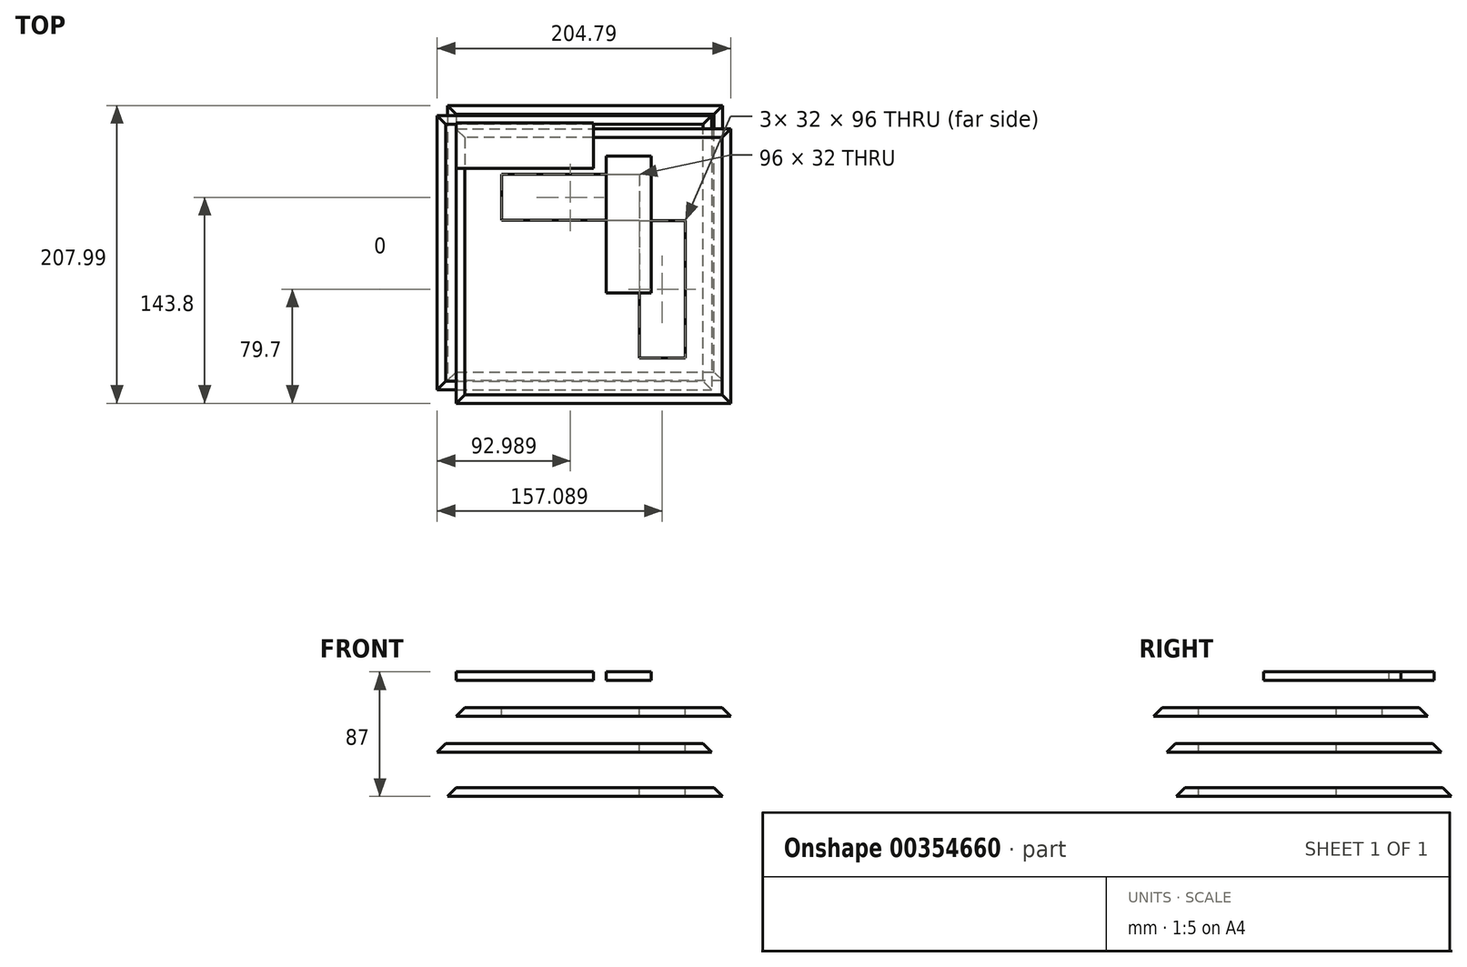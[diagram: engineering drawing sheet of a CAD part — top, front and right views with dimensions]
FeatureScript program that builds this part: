
annotation { "Feature Type Name" : "Feature", "Feature Type Description" : "" }
export const myFeature = defineFeature(function(context is Context, id is Id, definition is map)
    precondition{}
    {
        {
            var Q0;
            Q0=qCreatedBy(makeId("Top.planeOp"),FACE);
            var sketch = newSketch(context, id + "F0", { "sketchPlane" : qUnion([Q0])});
            skLineSegment(sketch, "E0.bottom", {"start": v(-110.78, 83.07) * mm, "end": v(81.22, 83.07) * mm});
            skLineSegment(sketch, "E0.top", {"start": v(-110.78, -108.93) * mm, "end": v(81.22, -108.93) * mm});
            skLineSegment(sketch, "E0.left", {"start": v(-110.78, 83.07) * mm, "end": v(-110.78, -108.93) * mm});
            skLineSegment(sketch, "E0.right", {"start": v(81.22, 83.07) * mm, "end": v(81.22, -108.93) * mm});
            skSolve(sketch);
        }
        {
            var Q0;
            Q0=makeQuery(id+"F0.imprint","IMPRINT",FACE,{"disambiguationData":[TD([[makeQuery(id+"F0.imprint","IMPRINT",EDGE,{"derivedFrom":sQuery(id+"F0.wireOp",EDGE,"E0.bottom")}),-1.0]])]});
            extrude(context, id + "F1", {"entities" : qUnion([Q0]), "depth" : 6 * mm});
        }
        {
            var Q0;
            Q0=makeQuery(id+"F1.opExtrude","CAP_FACE",FACE,{"disambiguationData":[OSD([sQuery(id+"F0.wireOp",EDGE,"E0.bottom"),sQuery(id+"F0.wireOp",EDGE,"E0.top"),sQuery(id+"F0.wireOp",EDGE,"E0.left"),sQuery(id+"F0.wireOp",EDGE,"E0.right")])],"isStart":false});
            chamfer(context, id + "F2", {"entities" : qUnion([Q0]), "width" : 6 * mm, "tangentPropagation" : true});
        }
        {
            var Q0;
            Q0=makeQuery(id+"F1.opExtrude","CAP_FACE",FACE,{"disambiguationData":[OSD([sQuery(id+"F0.wireOp",EDGE,"E0.bottom"),sQuery(id+"F0.wireOp",EDGE,"E0.top"),sQuery(id+"F0.wireOp",EDGE,"E0.left"),sQuery(id+"F0.wireOp",EDGE,"E0.right")])],"isStart":false});
            cPlane(context, id + "F3", {"entities" : qUnion([Q0]), "cplaneType" : CPlaneType.OFFSET, "offset" : 25 * mm, "width" : 150 * mm, "height" : 150 * mm});
        }
        {
            var Q0;
            Q0=qCreatedBy(id+"F3.planeOp",FACE);
            var sketch = newSketch(context, id + "F4", { "sketchPlane" : qUnion([Q0])});
            skLineSegment(sketch, "E1.bottom", {"start": v(-118.07, 76.11) * mm, "end": v(73.53, 76.11) * mm});
            skLineSegment(sketch, "E1.top", {"start": v(-118.07, -115.49) * mm, "end": v(73.53, -115.49) * mm});
            skLineSegment(sketch, "E1.left", {"start": v(-118.07, 76.11) * mm, "end": v(-118.07, -115.49) * mm});
            skLineSegment(sketch, "E1.right", {"start": v(73.53, 76.11) * mm, "end": v(73.53, -115.49) * mm});
            skSolve(sketch);
        }
        {
            var Q0;
            Q0=makeQuery(id+"F4.imprint","IMPRINT",FACE,{"disambiguationData":[TD([[makeQuery(id+"F4.imprint","IMPRINT",EDGE,{"derivedFrom":sQuery(id+"F4.wireOp",EDGE,"E1.bottom")}),-1.0]])]});
            extrude(context, id + "F5", {"entities" : qUnion([Q0]), "depth" : 6 * mm});
        }
        {
            var Q0;
            Q0=makeQuery(id+"F5.opExtrude","CAP_FACE",FACE,{"disambiguationData":[OSD([sQuery(id+"F4.wireOp",EDGE,"E1.bottom"),sQuery(id+"F4.wireOp",EDGE,"E1.top"),sQuery(id+"F4.wireOp",EDGE,"E1.left"),sQuery(id+"F4.wireOp",EDGE,"E1.right")])],"isStart":false});
            chamfer(context, id + "F6", {"entities" : qUnion([Q0]), "width" : 6 * mm, "tangentPropagation" : true});
        }
        {
            var Q0;
            Q0=qCreatedBy(id+"F3.planeOp",FACE);
            cPlane(context, id + "F7", {"entities" : qUnion([Q0]), "cplaneType" : CPlaneType.OFFSET, "offset" : 25 * mm, "width" : 150 * mm, "height" : 150 * mm});
        }
        {
            var Q0;
            Q0=qCreatedBy(id+"F7.planeOp",FACE);
            var sketch = newSketch(context, id + "F8", { "sketchPlane" : qUnion([Q0])});
            skLineSegment(sketch, "E2.bottom", {"start": v(-104.88, 66.68) * mm, "end": v(86.72, 66.68) * mm});
            skLineSegment(sketch, "E2.top", {"start": v(-104.88, -124.92) * mm, "end": v(86.72, -124.92) * mm});
            skLineSegment(sketch, "E2.left", {"start": v(-104.88, 66.68) * mm, "end": v(-104.88, -124.92) * mm});
            skLineSegment(sketch, "E2.right", {"start": v(86.72, 66.68) * mm, "end": v(86.72, -124.92) * mm});
            skSolve(sketch);
        }
        {
            var Q0;
            Q0 = qSketchRegion(id + "F8", true);
            extrude(context, id + "F9", {"entities" : qUnion([Q0]), "depth" : 6 * mm});
        }
        {
            var Q0;
            Q0=makeQuery(id+"F9.opExtrude","CAP_FACE",FACE,{"disambiguationData":[OSD([sQuery(id+"F8.wireOp",EDGE,"E2.bottom"),sQuery(id+"F8.wireOp",EDGE,"E2.top"),sQuery(id+"F8.wireOp",EDGE,"E2.left"),sQuery(id+"F8.wireOp",EDGE,"E2.right")])],"isStart":false});
            chamfer(context, id + "F10", {"entities" : qUnion([Q0]), "width" : 6 * mm, "tangentPropagation" : true});
        }
        {
            var Q0;
            Q0=makeQuery(id+"F9.opExtrude","CAP_FACE",FACE,{"disambiguationData":[OSD([sQuery(id+"F8.wireOp",EDGE,"E2.bottom"),sQuery(id+"F8.wireOp",EDGE,"E2.top"),sQuery(id+"F8.wireOp",EDGE,"E2.left"),sQuery(id+"F8.wireOp",EDGE,"E2.right")])],"isStart":false});
            var sketch = newSketch(context, id + "F11", { "sketchPlane" : qUnion([Q0])});
            skLineSegment(sketch, "E3.bottom", {"start": v(-73.08, 34.88) * mm, "end": v(22.92, 34.88) * mm});
            skLineSegment(sketch, "E3.top", {"start": v(-73.08, 2.88) * mm, "end": v(22.92, 2.88) * mm});
            skLineSegment(sketch, "E3.left", {"start": v(-73.08, 34.88) * mm, "end": v(-73.08, 2.88) * mm});
            skLineSegment(sketch, "E3.right", {"start": v(22.92, 34.88) * mm, "end": v(22.92, 2.88) * mm});
            skLineSegment(sketch, "E4.bottom", {"start": v(-41.28, 2.88) * mm, "end": v(-9.28, 2.88) * mm});
            skLineSegment(sketch, "E4.top", {"start": v(-41.28, -93.12) * mm, "end": v(-9.28, -93.12) * mm});
            skLineSegment(sketch, "E4.left", {"start": v(-41.28, 2.88) * mm, "end": v(-41.28, -93.12) * mm});
            skLineSegment(sketch, "E4.right", {"start": v(-9.28, 2.88) * mm, "end": v(-9.28, -93.12) * mm});
            skSolve(sketch);
        }
        {
            var Q0;
            Q0=makeQuery(id+"F11.imprint","IMPRINT",FACE,{"disambiguationData":[TD([[makeQuery(id+"F11.imprint","IMPRINT",EDGE,{"derivedFrom":sQuery(id+"F11.wireOp",EDGE,"E3.bottom")}),-1.0]])]});
            var Q1;
            Q1=makeQuery(id+"F11.imprint","IMPRINT",FACE,{"disambiguationData":[TD([[makeQuery(id+"F11.imprint","IMPRINT",EDGE,{"derivedFrom":sQuery(id+"F11.wireOp",EDGE,"E4.bottom")}),-1.0]])]});
            extrude(context, id + "F12", {"entities" : qUnion([Q0, Q1]), "operationType" : NewBodyOperationType.REMOVE, "oppositeDirection" : true, "depth" : 25 * mm});
        }
        {
            var Q0;
            Q0=makeQuery(id+"F9.opExtrude","CAP_FACE",FACE,{"disambiguationData":[OSD([sQuery(id+"F8.wireOp",EDGE,"E2.bottom"),sQuery(id+"F8.wireOp",EDGE,"E2.top"),sQuery(id+"F8.wireOp",EDGE,"E2.left"),sQuery(id+"F8.wireOp",EDGE,"E2.right")])],"isStart":false});
            var sketch = newSketch(context, id + "F13", { "sketchPlane" : qUnion([Q0])});
            skLineSegment(sketch, "E5.bottom", {"start": v(23.02, 2.78) * mm, "end": v(55.02, 2.78) * mm});
            skLineSegment(sketch, "E5.top", {"start": v(23.02, -93.22) * mm, "end": v(55.02, -93.22) * mm});
            skLineSegment(sketch, "E5.left", {"start": v(23.02, 2.78) * mm, "end": v(23.02, -93.22) * mm});
            skLineSegment(sketch, "E5.right", {"start": v(55.02, 2.78) * mm, "end": v(55.02, -93.22) * mm});
            skSolve(sketch);
        }
        {
            var Q0;
            Q0 = qSketchRegion(id + "F13", true);
            extrude(context, id + "F14", {"entities" : qUnion([Q0]), "operationType" : NewBodyOperationType.REMOVE, "endBound" : BoundingType.THROUGH_ALL, "oppositeDirection" : true, "depth" : 25 * mm});
        }
        {
            var Q0;
            Q0=qCreatedBy(id+"F7.planeOp",FACE);
            cPlane(context, id + "F15", {"entities" : qUnion([Q0]), "cplaneType" : CPlaneType.OFFSET, "offset" : 25 * mm, "width" : 150 * mm, "height" : 150 * mm});
        }
        {
            var Q0;
            Q0=qCreatedBy(id+"F15.planeOp",FACE);
            var sketch = newSketch(context, id + "F16", { "sketchPlane" : qUnion([Q0])});
            skLineSegment(sketch, "E6.bottom", {"start": v(-104.83, 70.97) * mm, "end": v(-9.13, 70.97) * mm});
            skLineSegment(sketch, "E6.top", {"start": v(-104.83, 39.27) * mm, "end": v(-9.13, 39.27) * mm});
            skLineSegment(sketch, "E6.left", {"start": v(-104.83, 70.97) * mm, "end": v(-104.83, 39.27) * mm});
            skLineSegment(sketch, "E6.right", {"start": v(-9.13, 70.97) * mm, "end": v(-9.13, 39.27) * mm});
            skLineSegment(sketch, "E7.bottom", {"start": v(-72.83, 39.27) * mm, "end": v(-41.13, 39.27) * mm});
            skLineSegment(sketch, "E7.top", {"start": v(-72.83, -56.43) * mm, "end": v(-41.13, -56.43) * mm});
            skLineSegment(sketch, "E7.left", {"start": v(-72.83, 39.27) * mm, "end": v(-72.83, -56.43) * mm});
            skLineSegment(sketch, "E7.right", {"start": v(-41.13, 39.27) * mm, "end": v(-41.13, -56.43) * mm});
            skLineSegment(sketch, "E8.bottom", {"start": v(-0.24, 47.86) * mm, "end": v(31.46, 47.86) * mm});
            skLineSegment(sketch, "E8.top", {"start": v(-0.24, -47.84) * mm, "end": v(31.46, -47.84) * mm});
            skLineSegment(sketch, "E8.left", {"start": v(-0.24, 47.86) * mm, "end": v(-0.24, -47.84) * mm});
            skLineSegment(sketch, "E8.right", {"start": v(31.46, 47.86) * mm, "end": v(31.46, -47.84) * mm});
            skSolve(sketch);
        }
        {
            var Q0;
            Q0=makeQuery(id+"F16.imprint","IMPRINT",FACE,{"disambiguationData":[TD([[makeQuery(id+"F16.imprint","IMPRINT",EDGE,{"derivedFrom":sQuery(id+"F16.wireOp",EDGE,"E6.bottom")}),-1.0]])]});
            var Q1;
            Q1=makeQuery(id+"F16.imprint","IMPRINT",FACE,{"disambiguationData":[TD([[makeQuery(id+"F16.imprint","IMPRINT",EDGE,{"derivedFrom":sQuery(id+"F16.wireOp",EDGE,"E7.bottom")}),-1.0]])]});
            var Q2;
            Q2=makeQuery(id+"F16.imprint","IMPRINT",FACE,{"disambiguationData":[TD([[makeQuery(id+"F16.imprint","IMPRINT",EDGE,{"derivedFrom":sQuery(id+"F16.wireOp",EDGE,"E8.bottom")}),-1.0]])]});
            extrude(context, id + "F17", {"entities" : qUnion([Q0, Q1, Q2]), "depth" : 6 * mm});
        }
    });
